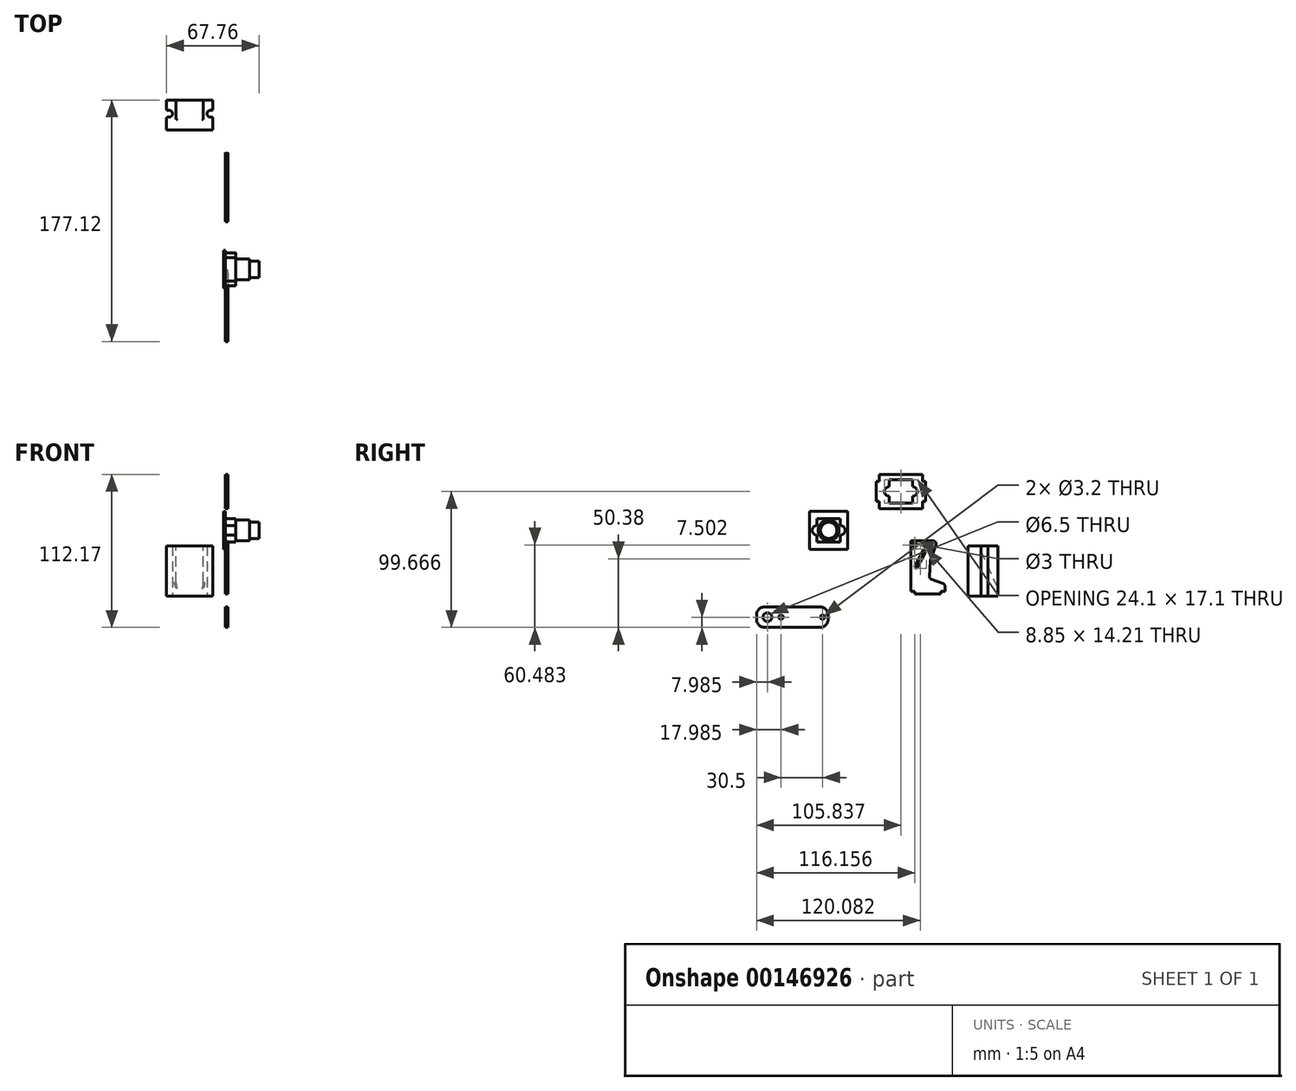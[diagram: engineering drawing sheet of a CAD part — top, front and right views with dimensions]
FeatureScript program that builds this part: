
annotation { "Feature Type Name" : "Feature", "Feature Type Description" : "" }
export const myFeature = defineFeature(function(context is Context, id is Id, definition is map)
    precondition{}
    {
        {
            var Q0;
            Q0=qCreatedBy(makeId("Top.planeOp"),FACE);
            var sketch = newSketch(context, id + "F0", { "sketchPlane" : qUnion([Q0])});
            skArc(sketch, "E0", {"start": v(-41.84, 12.4) * mm, "mid": v(-38.71, 14.88) * mm, "end": v(-41.84, 17.37) * mm});
            skArc(sketch, "E1", {"start": v(-10.29, 17.37) * mm, "mid": v(-13.41, 14.88) * mm, "end": v(-10.29, 12.4) * mm});
            skLineSegment(sketch, "E2.bottom", {"start": v(-43.06, 24.88) * mm, "end": v(-9.06, 24.88) * mm});
            skLineSegment(sketch, "E2.top", {"start": v(-43.06, 2.92) * mm, "end": v(-9.06, 2.92) * mm});
            skLineSegment(sketch, "E2.left", {"start": v(-43.06, 24.88) * mm, "end": v(-43.06, 18.34) * mm});
            skLineSegment(sketch, "E2.right", {"start": v(-9.06, 24.88) * mm, "end": v(-9.06, 18.34) * mm});
            skLineSegment(sketch, "E3", {"start": v(-41.26, 14.88) * mm, "end": v(-10.86, 14.88) * mm, "construction": true});
            skLineSegment(sketch, "E4", {"start": v(-26.06, 14.88) * mm, "end": v(-26.06, 8.65) * mm, "construction": true});
            skLineSegment(sketch, "E5.trimOffspring", {"start": v(-43.06, 11.42) * mm, "end": v(-43.06, 2.92) * mm});
            skLineSegment(sketch, "E6.trimOffspring", {"start": v(-9.06, 11.42) * mm, "end": v(-9.06, 2.92) * mm});
            skPoint(sketch, "E7.visualSharp", {"position": v(-43.06, 16.69) * mm});
            skArc(sketch, "E7.filletArc", {"start": v(-43.06, 18.34) * mm, "mid": v(-42.69, 17.56) * mm, "end": v(-41.84, 17.37) * mm});
            skPoint(sketch, "E8.visualSharp", {"position": v(-43.06, 13.07) * mm});
            skArc(sketch, "E8.filletArc", {"start": v(-41.84, 12.4) * mm, "mid": v(-42.69, 12.2) * mm, "end": v(-43.06, 11.42) * mm});
            skPoint(sketch, "E9.visualSharp", {"position": v(-9.06, 13.07) * mm});
            skArc(sketch, "E9.filletArc", {"start": v(-9.06, 11.42) * mm, "mid": v(-9.44, 12.2) * mm, "end": v(-10.29, 12.4) * mm});
            skPoint(sketch, "E10.visualSharp", {"position": v(-9.06, 16.69) * mm});
            skArc(sketch, "E10.filletArc", {"start": v(-10.29, 17.37) * mm, "mid": v(-9.44, 17.56) * mm, "end": v(-9.06, 18.34) * mm});
            skSolve(sketch);
        }
        {
            var Q0;
            Q0=makeQuery(id+"F0.imprint","IMPRINT",FACE,{"disambiguationData":[TD([[makeQuery(id+"F0.imprint","IMPRINT",EDGE,{"derivedFrom":sQuery(id+"F0.wireOp",EDGE,"E0")}),-1.0]])]});
            extrude(context, id + "F1", {"entities" : qUnion([Q0]), "depth" : 37 * mm});
        }
        {
            var Q0;
            Q0=makeQuery(id+"F1.opExtrude","SWEPT_FACE",FACE,{"disambiguationData":[OSD([sQuery(id+"F0.wireOp",EDGE,"E5.trimOffspring")])]});
            cPlane(context, id + "F2", {"entities" : qUnion([Q0]), "cplaneType" : CPlaneType.OFFSET, "offset" : 17 * mm, "oppositeDirection" : true, "width" : 150 * mm, "height" : 150 * mm});
        }
        {
            var Q0;
            Q0=qCreatedBy(id+"F2.planeOp",FACE);
            var sketch = newSketch(context, id + "F3", { "sketchPlane" : qUnion([Q0])});
            skLineSegment(sketch, "E11", {"start": v(-29.88, -5) * mm, "end": v(-62.05, -5) * mm});
            skLineSegment(sketch, "E12", {"start": v(-29.88, -5) * mm, "end": v(-7.96, 42) * mm});
            skLineSegment(sketch, "E13", {"start": v(-62.05, 42) * mm, "end": v(-7.96, 42) * mm});
            skLineSegment(sketch, "E14", {"start": v(-62.05, 42) * mm, "end": v(-62.05, -5) * mm});
            skSolve(sketch);
        }
        {
            var Q0;
            Q0 = qSketchRegion(id + "F3", true);
            extrude(context, id + "F4", {"entities" : qUnion([Q0]), "operationType" : NewBodyOperationType.REMOVE, "endBound" : BoundingType.SYMMETRIC, "oppositeDirection" : true, "depth" : 20 * mm});
        }
        {
            var Q0;
            Q0=makeQuery(id+"F4.boolean.opBoolean","COPY",FACE,{"derivedFrom":makeQuery(id+"F4.opExtrude","SWEPT_FACE",FACE,{"disambiguationData":[OSD([sQuery(id+"F3.wireOp",EDGE,"E12")])]})});
            var Q1;
            Q1=makeQuery(id+"F4.boolean.opBoolean","COPY",FACE,{"derivedFrom":makeQuery(id+"F4.opExtrude","CAP_FACE",FACE,{"disambiguationData":[OSD([sQuery(id+"F3.wireOp",EDGE,"E11"),sQuery(id+"F3.wireOp",EDGE,"E12"),sQuery(id+"F3.wireOp",EDGE,"E13"),sQuery(id+"F3.wireOp",EDGE,"E14")])],"isStart":false})});
            var Q2;
            Q2=makeQuery(id+"F4.boolean.opBoolean","COPY",FACE,{"derivedFrom":makeQuery(id+"F4.opExtrude","CAP_FACE",FACE,{"disambiguationData":[OSD([sQuery(id+"F3.wireOp",EDGE,"E11"),sQuery(id+"F3.wireOp",EDGE,"E12"),sQuery(id+"F3.wireOp",EDGE,"E13"),sQuery(id+"F3.wireOp",EDGE,"E14")])],"isStart":true})});
            fillet(context, id + "F5", {"entities" : qUnion([Q0, Q1, Q2]), "radius" : 1 * mm, "allowEdgeOverflow" : false});
        }
        {
            var Q0;
            Q0=qCreatedBy(makeId("Right.planeOp"),FACE);
            var sketch = newSketch(context, id + "F6", { "sketchPlane" : qUnion([Q0])});
            skLineSegment(sketch, "E15.bottom", {"start": v(-39.08, 40.58) * mm, "end": v(-26.58, 40.58) * mm});
            skLineSegment(sketch, "E15.top", {"start": v(-39.08, 3.58) * mm, "end": v(-36.08, 3.58) * mm});
            skLineSegment(sketch, "E15.left", {"start": v(-39.08, 40.58) * mm, "end": v(-39.08, 3.58) * mm});
            skLineSegment(sketch, "E15.right", {"start": v(-14.08, 7.27) * mm, "end": v(-14.08, 3.58) * mm});
            skLineSegment(sketch, "E16", {"start": v(-36.08, 3.58) * mm, "end": v(-36.08, 1.58) * mm});
            skLineSegment(sketch, "E17", {"start": v(-36.08, 1.58) * mm, "end": v(-17.08, 1.58) * mm});
            skLineSegment(sketch, "E18", {"start": v(-17.08, 1.58) * mm, "end": v(-17.08, 3.58) * mm});
            skLineSegment(sketch, "E19.trimOffspring", {"start": v(-17.08, 3.58) * mm, "end": v(-14.08, 3.58) * mm});
            skLineSegment(sketch, "E20", {"start": v(-29.54, 34.58) * mm, "end": v(-36.58, 21.34) * mm});
            skLineSegment(sketch, "E21", {"start": v(-36.58, 21.34) * mm, "end": v(-34.77, 20.38) * mm});
            skLineSegment(sketch, "E22", {"start": v(-34.77, 20.38) * mm, "end": v(-27.73, 33.62) * mm});
            skLineSegment(sketch, "E23", {"start": v(-27.73, 33.62) * mm, "end": v(-29.54, 34.58) * mm});
            skCircle(sketch, "E24", {"center": v(-36.08, 37.58) * mm, "radius": 1.5 * mm});
            skLineSegment(sketch, "E25", {"start": v(-35.68, 26.46) * mm, "end": v(-29.14, 22.98) * mm, "construction": true});
            skLineSegment(sketch, "E26", {"start": v(-24.66, 26.12) * mm, "end": v(-25.4, 14.45) * mm});
            skLineSegment(sketch, "E27", {"start": v(-24.11, 12.44) * mm, "end": v(-15.38, 9.14) * mm});
            skPoint(sketch, "E28.orphan", {"position": v(-14.08, 40.58) * mm});
            skPoint(sketch, "E29.center.orphan", {"position": v(-17.08, 37.58) * mm});
            skPoint(sketch, "E30.visualSharp", {"position": v(-26.9, 34.05) * mm});
            skPoint(sketch, "E31.visualSharp", {"position": v(-24.18, 33.62) * mm});
            skPoint(sketch, "E32.visualSharp", {"position": v(-25.5, 12.97) * mm});
            skArc(sketch, "E32.filletArc", {"start": v(-25.4, 14.45) * mm, "mid": v(-25.09, 13.23) * mm, "end": v(-24.11, 12.44) * mm});
            skPoint(sketch, "E33.visualSharp", {"position": v(-14.08, 8.65) * mm});
            skArc(sketch, "E33.filletArc", {"start": v(-14.08, 7.27) * mm, "mid": v(-14.44, 8.4) * mm, "end": v(-15.38, 9.14) * mm});
            skLineSegment(sketch, "E34", {"start": v(-24.66, 26.12) * mm, "end": v(-20.77, 37.96) * mm});
            skLineSegment(sketch, "E35", {"start": v(-26.58, 40.58) * mm, "end": v(-22.67, 40.58) * mm});
            skPoint(sketch, "E36.visualSharp", {"position": v(-19.9, 40.58) * mm});
            skArc(sketch, "E36.filletArc", {"start": v(-20.77, 37.96) * mm, "mid": v(-21.04, 39.76) * mm, "end": v(-22.67, 40.58) * mm});
            skSolve(sketch);
        }
        {
            var Q0;
            Q0 = qSketchRegion(id + "F6", true);
            extrude(context, id + "F7", {"entities" : qUnion([Q0]), "depth" : 2 * mm});
        }
        {
            var Q0;
            Q0=qCreatedBy(makeId("Right.planeOp"),FACE);
            var sketch = newSketch(context, id + "F8", { "sketchPlane" : qUnion([Q0])});
            skLineSegment(sketch, "E37.bottom", {"start": v(-62.4, 64.27) * mm, "end": v(-30.4, 64.27) * mm});
            skLineSegment(sketch, "E37.top", {"start": v(-62.4, 89.27) * mm, "end": v(-30.4, 89.27) * mm});
            skLineSegment(sketch, "E37.left", {"start": v(-62.4, 64.27) * mm, "end": v(-62.4, 69.42) * mm});
            skLineSegment(sketch, "E37.right", {"start": v(-30.4, 64.27) * mm, "end": v(-30.4, 69.42) * mm});
            skLineSegment(sketch, "E38", {"start": v(-30.4, 84.12) * mm, "end": v(-28.4, 84.12) * mm});
            skLineSegment(sketch, "E39", {"start": v(-28.4, 84.12) * mm, "end": v(-28.4, 69.42) * mm});
            skLineSegment(sketch, "E40", {"start": v(-28.4, 69.42) * mm, "end": v(-30.4, 69.42) * mm});
            skLineSegment(sketch, "E41", {"start": v(-46.4, 89.27) * mm, "end": v(-46.4, 64.27) * mm, "construction": true});
            skLineSegment(sketch, "E42.MirrorCS", {"start": v(-62.4, 84.12) * mm, "end": v(-64.4, 84.12) * mm});
            skLineSegment(sketch, "E43.MirrorCS", {"start": v(-64.4, 69.42) * mm, "end": v(-62.4, 69.42) * mm});
            skLineSegment(sketch, "E44.MirrorCS", {"start": v(-64.4, 84.12) * mm, "end": v(-64.4, 69.42) * mm});
            skLineSegment(sketch, "E45.bottom", {"start": v(-37.85, 85.32) * mm, "end": v(-54.95, 85.32) * mm});
            skLineSegment(sketch, "E45.top", {"start": v(-37.85, 68.22) * mm, "end": v(-54.95, 68.22) * mm});
            skLineSegment(sketch, "E45.left", {"start": v(-37.85, 85.32) * mm, "end": v(-37.85, 80.27) * mm});
            skLineSegment(sketch, "E45.right", {"start": v(-54.95, 85.32) * mm, "end": v(-54.95, 80.27) * mm});
            skPoint(sketch, "E45.middle", {"position": v(-46.4, 76.77) * mm});
            skArc(sketch, "E46", {"start": v(-54.95, 80.27) * mm, "mid": v(-58.45, 76.77) * mm, "end": v(-54.95, 73.27) * mm});
            skArc(sketch, "E47", {"start": v(-37.85, 73.27) * mm, "mid": v(-34.35, 76.77) * mm, "end": v(-37.85, 80.27) * mm});
            skLineSegment(sketch, "E48.trimOffspring", {"start": v(-54.95, 73.27) * mm, "end": v(-54.95, 68.22) * mm});
            skLineSegment(sketch, "E49.trimOffspring", {"start": v(-37.85, 73.27) * mm, "end": v(-37.85, 68.22) * mm});
            skLineSegment(sketch, "E50.trimOffspring", {"start": v(-62.4, 84.12) * mm, "end": v(-62.4, 89.27) * mm});
            skLineSegment(sketch, "E51.trimOffspring", {"start": v(-30.4, 84.12) * mm, "end": v(-30.4, 89.27) * mm});
            skSolve(sketch);
        }
        {
            var Q0;
            Q0 = qSketchRegion(id + "F8", true);
            extrude(context, id + "F9", {"entities" : qUnion([Q0]), "depth" : 2 * mm});
        }
        {
            var Q0;
            Q0=qCreatedBy(makeId("Right.planeOp"),FACE);
            var sketch = newSketch(context, id + "F10", { "sketchPlane" : qUnion([Q0])});
            skLineSegment(sketch, "E52", {"start": v(-99.35, 60.8) * mm, "end": v(-99.35, 35.8) * mm, "construction": true});
            skLineSegment(sketch, "E53.bottom", {"start": v(-90.8, 56.84) * mm, "end": v(-107.9, 56.84) * mm});
            skLineSegment(sketch, "E53.top", {"start": v(-90.8, 39.74) * mm, "end": v(-107.9, 39.74) * mm});
            skLineSegment(sketch, "E53.left", {"start": v(-90.8, 56.84) * mm, "end": v(-90.8, 51.8) * mm});
            skLineSegment(sketch, "E53.right", {"start": v(-107.9, 56.84) * mm, "end": v(-107.9, 51.8) * mm});
            skPoint(sketch, "E53.middle", {"position": v(-99.35, 48.3) * mm});
            skArc(sketch, "E54", {"start": v(-107.9, 51.8) * mm, "mid": v(-111.4, 48.3) * mm, "end": v(-107.9, 44.8) * mm});
            skArc(sketch, "E55", {"start": v(-90.8, 44.8) * mm, "mid": v(-87.3, 48.3) * mm, "end": v(-90.8, 51.8) * mm});
            skLineSegment(sketch, "E56.trimOffspring", {"start": v(-107.9, 44.8) * mm, "end": v(-107.9, 39.74) * mm});
            skLineSegment(sketch, "E57.trimOffspring", {"start": v(-90.8, 44.8) * mm, "end": v(-90.8, 39.74) * mm});
            skSolve(sketch);
        }
        {
            var Q0;
            Q0=makeQuery(id+"F10.imprint","IMPRINT",FACE,{"disambiguationData":[TD([[makeQuery(id+"F10.imprint","IMPRINT",EDGE,{"derivedFrom":sQuery(id+"F10.wireOp",EDGE,"E53.bottom")}),1.0]])]});
            extrude(context, id + "F11", {"entities" : qUnion([Q0]), "depth" : 7.7 * mm});
        }
        {
            var Q0;
            Q0=makeQuery(id+"F11.opExtrude","CAP_FACE",FACE,{"disambiguationData":[OSD([sQuery(id+"F10.wireOp",EDGE,"E53.bottom"),sQuery(id+"F10.wireOp",EDGE,"E53.top"),sQuery(id+"F10.wireOp",EDGE,"E53.left"),sQuery(id+"F10.wireOp",EDGE,"E53.right"),sQuery(id+"F10.wireOp",EDGE,"E54"),sQuery(id+"F10.wireOp",EDGE,"E55"),sQuery(id+"F10.wireOp",EDGE,"E56.trimOffspring"),sQuery(id+"F10.wireOp",EDGE,"E57.trimOffspring")])],"isStart":false});
            var sketch = newSketch(context, id + "F12", { "sketchPlane" : qUnion([Q0])});
            skLineSegment(sketch, "E58", {"start": v(-107.9, 56.84) * mm, "end": v(-90.8, 39.74) * mm, "construction": true});
            skLineSegment(sketch, "E59", {"start": v(-90.8, 39.74) * mm, "end": v(-90.8, 56.84) * mm, "construction": true});
            skLineSegment(sketch, "E60", {"start": v(-90.8, 56.84) * mm, "end": v(-107.9, 39.74) * mm, "construction": true});
            skCircle(sketch, "E61", {"center": v(-99.35, 48.3) * mm, "radius": 7.6 * mm});
            skSolve(sketch);
        }
        {
            var Q0;
            Q0 = qSketchRegion(id + "F12", true);
            extrude(context, id + "F13", {"entities" : qUnion([Q0]), "operationType" : NewBodyOperationType.ADD, "depth" : 10 * mm});
        }
        {
            var Q0;
            Q0=makeQuery(id+"F13.opExtrude","CAP_FACE",FACE,{"disambiguationData":[OSD([sQuery(id+"F12.wireOp",EDGE,"E61")])],"isStart":false});
            var sketch = newSketch(context, id + "F14", { "sketchPlane" : qUnion([Q0])});
            skCircle(sketch, "E62", {"center": v(-99.35, 48.3) * mm, "radius": 6 * mm});
            skSolve(sketch);
        }
        {
            var Q0;
            Q0 = qSketchRegion(id + "F14", true);
            extrude(context, id + "F15", {"entities" : qUnion([Q0]), "operationType" : NewBodyOperationType.ADD, "depth" : 7 * mm});
        }
        {
            var Q0;
            Q0=makeQuery(id+"F11.opExtrude","CAP_FACE",FACE,{"disambiguationData":[OSD([sQuery(id+"F10.wireOp",EDGE,"E53.bottom"),sQuery(id+"F10.wireOp",EDGE,"E53.top"),sQuery(id+"F10.wireOp",EDGE,"E53.left"),sQuery(id+"F10.wireOp",EDGE,"E53.right"),sQuery(id+"F10.wireOp",EDGE,"E54"),sQuery(id+"F10.wireOp",EDGE,"E55"),sQuery(id+"F10.wireOp",EDGE,"E56.trimOffspring"),sQuery(id+"F10.wireOp",EDGE,"E57.trimOffspring")])],"isStart":true});
            var sketch = newSketch(context, id + "F16", { "sketchPlane" : qUnion([Q0])});
            skLineSegment(sketch, "E63.bottom", {"start": v(113.25, 62.2) * mm, "end": v(85.45, 62.2) * mm});
            skLineSegment(sketch, "E63.top", {"start": v(113.25, 34.4) * mm, "end": v(85.45, 34.4) * mm});
            skLineSegment(sketch, "E63.left", {"start": v(113.25, 62.2) * mm, "end": v(113.25, 34.4) * mm});
            skLineSegment(sketch, "E63.right", {"start": v(85.45, 62.2) * mm, "end": v(85.45, 34.4) * mm});
            skSolve(sketch);
        }
        {
            var Q0;
            Q0 = qSketchRegion(id + "F16", true);
            extrude(context, id + "F17", {"entities" : qUnion([Q0]), "operationType" : NewBodyOperationType.ADD, "depth" : 1.2 * mm});
        }
        {
            var Q0;
            Q0=qCreatedBy(makeId("Right.planeOp"),FACE);
            var sketch = newSketch(context, id + "F18", { "sketchPlane" : qUnion([Q0])});
            skLineSegment(sketch, "E64.bottom", {"start": v(-105.75, -7.9) * mm, "end": v(-146.24, -7.9) * mm});
            skLineSegment(sketch, "E64.top", {"start": v(-105.75, -22.9) * mm, "end": v(-146.24, -22.9) * mm});
            skLineSegment(sketch, "E64.left", {"start": v(-99.75, -13.9) * mm, "end": v(-99.75, -16.9) * mm});
            skLineSegment(sketch, "E64.right", {"start": v(-152.24, -13.9) * mm, "end": v(-152.24, -16.9) * mm});
            skCircle(sketch, "E65", {"center": v(-144.25, -15.4) * mm, "radius": 3.25 * mm});
            skCircle(sketch, "E66", {"center": v(-103.75, -15.4) * mm, "radius": 1.6 * mm});
            skCircle(sketch, "E67", {"center": v(-134.25, -15.4) * mm, "radius": 1.6 * mm});
            skPoint(sketch, "E68.visualSharp", {"position": v(-99.75, -7.9) * mm});
            skArc(sketch, "E68.filletArc", {"start": v(-99.75, -13.9) * mm, "mid": v(-101.51, -9.66) * mm, "end": v(-105.75, -7.9) * mm});
            skPoint(sketch, "E69.visualSharp", {"position": v(-99.75, -22.9) * mm});
            skArc(sketch, "E69.filletArc", {"start": v(-105.75, -22.9) * mm, "mid": v(-101.51, -21.14) * mm, "end": v(-99.75, -16.9) * mm});
            skPoint(sketch, "E70.visualSharp", {"position": v(-152.24, -22.9) * mm});
            skArc(sketch, "E70.filletArc", {"start": v(-152.24, -16.9) * mm, "mid": v(-150.48, -21.14) * mm, "end": v(-146.24, -22.9) * mm});
            skPoint(sketch, "E71.visualSharp", {"position": v(-152.24, -7.9) * mm});
            skArc(sketch, "E71.filletArc", {"start": v(-146.24, -7.9) * mm, "mid": v(-150.48, -9.66) * mm, "end": v(-152.24, -13.9) * mm});
            skSolve(sketch);
        }
        {
            var Q0;
            Q0=makeQuery(id+"F18.imprint","IMPRINT",FACE,{"disambiguationData":[TD([[makeQuery(id+"F18.imprint","IMPRINT",EDGE,{"derivedFrom":sQuery(id+"F18.wireOp",EDGE,"E64.bottom")}),1.0]])]});
            extrude(context, id + "F19", {"entities" : qUnion([Q0]), "depth" : 2 * mm});
        }
    });
